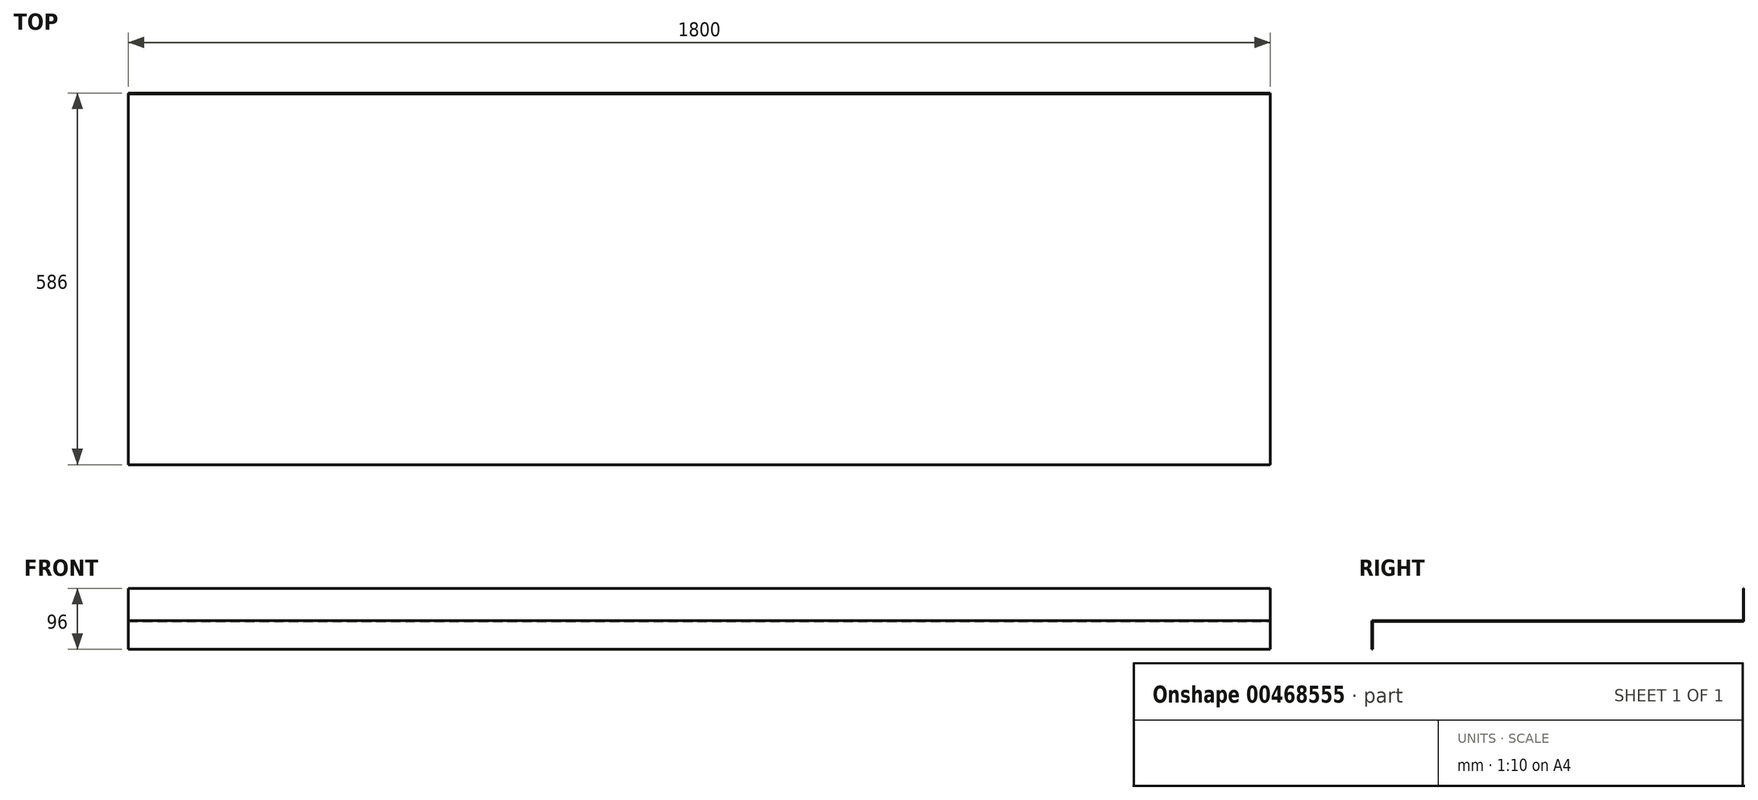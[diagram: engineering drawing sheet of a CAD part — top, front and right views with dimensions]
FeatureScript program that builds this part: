
annotation { "Feature Type Name" : "Feature", "Feature Type Description" : "" }
export const myFeature = defineFeature(function(context is Context, id is Id, definition is map)
    precondition{}
    {
        {
            var Q0;
            Q0=qCreatedBy(makeId("Top.planeOp"),FACE);
            var sketch = newSketch(context, id + "F0", { "sketchPlane" : qUnion([Q0])});
            skLineSegment(sketch, "E0.bottom", {"start": v(-477.38, 281.65) * mm, "end": v(1322.62, 281.65) * mm});
            skLineSegment(sketch, "E0.top", {"start": v(-477.38, -304.35) * mm, "end": v(1322.62, -304.35) * mm});
            skLineSegment(sketch, "E0.left", {"start": v(-477.38, 281.65) * mm, "end": v(-477.38, -304.35) * mm});
            skLineSegment(sketch, "E0.right", {"start": v(1322.62, 281.65) * mm, "end": v(1322.62, -304.35) * mm});
            skLineSegment(sketch, "E1.top", {"start": v(-477.38, 280.65) * mm, "end": v(1322.62, 280.65) * mm});
            skLineSegment(sketch, "E1.left", {"start": v(-477.38, 281.65) * mm, "end": v(-477.38, 280.65) * mm});
            skLineSegment(sketch, "E1.right", {"start": v(1322.62, 281.65) * mm, "end": v(1322.62, 280.65) * mm});
            skSolve(sketch);
        }
        {
            var Q0;
            Q0=makeQuery(id+"F0.imprint","IMPRINT",FACE,{"disambiguationData":[TD([[makeQuery(id+"F0.imprint","IMPRINT",EDGE,{"derivedFrom":sQuery(id+"F0.wireOp",EDGE,"E0.top")}),1.0]])]});
            extrude(context, id + "F1", {"entities" : qUnion([Q0]), "depth" : 1 * mm, "offsetDistance" : 25 * mm});
        }
        {
            var Q0;
            Q0=makeQuery(id+"F0.imprint","IMPRINT",FACE,{"disambiguationData":[TD([[makeQuery(id+"F0.imprint","IMPRINT",EDGE,{"derivedFrom":sQuery(id+"F0.wireOp",EDGE,"E0.bottom")}),-1.0]])]});
            extrude(context, id + "F2", {"entities" : qUnion([Q0]), "operationType" : NewBodyOperationType.ADD, "depth" : 52 * mm, "offsetDistance" : 25 * mm});
        }
        {
            var Q0;
            {var subQ0=sQuery(id+"F0.wireOp",EDGE,"E1.top");Q0=makeQuery(id+"F2.boolean.opBoolean","MERGE",FACE,{"derivedFrom":[makeQuery(id+"F1.opExtrude","CAP_FACE",FACE,{"disambiguationData":[OSD([sQuery(id+"F0.wireOp",EDGE,"E0.top"),sQuery(id+"F0.wireOp",EDGE,"E0.left"),sQuery(id+"F0.wireOp",EDGE,"E0.right"),subQ0])],"isStart":true}),makeQuery(id+"F2.opExtrude","CAP_FACE",FACE,{"disambiguationData":[OSD([sQuery(id+"F0.wireOp",EDGE,"E0.bottom"),subQ0,sQuery(id+"F0.wireOp",EDGE,"E1.left"),sQuery(id+"F0.wireOp",EDGE,"E1.right")])],"isStart":true})]});}
            var sketch = newSketch(context, id + "F3", { "sketchPlane" : qUnion([Q0])});
            skLineSegment(sketch, "E2.bottom", {"start": v(-477.38, 304.35) * mm, "end": v(1322.62, 304.35) * mm});
            skLineSegment(sketch, "E2.top", {"start": v(-477.38, 303.35) * mm, "end": v(1322.62, 303.35) * mm});
            skLineSegment(sketch, "E2.left", {"start": v(-477.38, 304.35) * mm, "end": v(-477.38, 303.35) * mm});
            skLineSegment(sketch, "E2.right", {"start": v(1322.62, 304.35) * mm, "end": v(1322.62, 303.35) * mm});
            skSolve(sketch);
        }
        {
            var Q0;
            Q0 = qSketchRegion(id + "F3", true);
            extrude(context, id + "F4", {"entities" : qUnion([Q0]), "operationType" : NewBodyOperationType.ADD, "depth" : 44 * mm, "offsetDistance" : 25 * mm});
        }
    });
